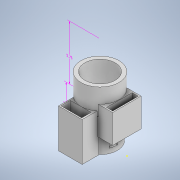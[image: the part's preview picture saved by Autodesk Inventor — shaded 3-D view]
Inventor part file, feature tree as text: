
AUTODESK INVENTOR PART (.ipt)
format: ipt  version: 2021 (Build 250183000, 183)  size: 472,064 bytes
history: native  units: in
note: dims shown in document units (in); Inventor stores cm internally (conversion verified against a paired STEP export)
features: sketch x24, extrude x14, other x3, plane x3, fillet x1
ambient origin geometry x8: Origin, YZ Plane, XZ Plane, XY Plane, X Axis, Y Axis, Z Axis, Center Point
bodies: Solid1 (feature_tree)
feature tree (45):
  other  "Annotations"
  extrude  "Extrusion1"  Depth=3.5433in TaperAngle=0.0deg
  extrude  "Extrusion2"  Depth=5.75in TaperAngle=0.0deg
  sketch  "Sketch4"  dims[d34=5.575in d35=0.0in d58=0.0787in]
  sketch  "Sketch5"  dims[d59=1.25in d60=4.1in]
  sketch  "Sketch6"  dims[d61=1.25in d62=4.1in]
  fillet  "Fillet1"  Radius=3.2in
  plane  "Work Plane2"
  extrude  "Extrusion4"  Depth=0.6875in TaperAngle=0.0deg
  sketch  "Sketch12"  dims[d67=2.2in d68=1.0in]
  sketch  "Sketch13"  dims[d69=3.8625in d70=0.0in d71=1.0in]
  extrude  "Extrusion8"  Depth=0.0787in
  plane  "Work Plane4"
  sketch  "Sketch24"  dims[d74=1.825in d75=0.0in d76=1.25in]
  extrude  "Extrusion13"  Depth=4.1in
  extrude  "Extrusion14"  Depth=4.1in
  sketch  "Sketch27"  dims[d81=1.0in d82=0.0in d83=1.875in d84=0.0in]
  sketch  "Sketch28"  dims[d85=0.65in]
  extrude  "Extrusion15"  Depth=1.7625in TaperAngle=0.0deg
  extrude  "Extrusion16"  Depth=1.0in
  plane  "Work Plane5"
  extrude  "Extrusion17"  Depth=1.0in
  sketch  "Sketch32"  dims[d91=3.0in d92=0.0in]
  extrude  "Extrusion18"  Depth=1.5in
  extrude  "Extrusion3"  Depth=1.25in
  extrude  "Extrusion19"  Depth=1.5in
  sketch  "Sketch35"  dims[d18=0.0344in]
  extrude  "Extrusion20"  Depth=1.5in
  extrude  "Extrusion21"  Depth=1.875in TaperAngle=0.0deg
  sketch  "Sketch1"  dims[d0=3.6614in d1=3.5433in d2=0.0in]
  sketch  "Sketch2"  dims[d3=4.0in d4=5.75in d5=0.0in d6=3.2in]
  sketch  "Sketch3"  dims[d7=9.0in d8=0.0in d11=0.6875in d12=0.0in]
  sketch  "Sketch7"  dims[d63=1.3in d64=0.0in d65=1.7625in d66=0.0in]
  sketch  "Sketch14"  dims[d72=0.6in d73=1.5in]
  sketch  "Sketch25"  dims[d77=3.0in d78=1.5in]
  sketch  "Sketch26"  dims[d79=3.0in d80=1.5in]
  sketch  "Sketch29"  dims[d86=2.7in]
  sketch  "Sketch30"  dims[d87=2.8125in d88=0.0in]
  sketch  "Sketch31"  dims[d89=2.8125in d90=0.0in]
  sketch  "Sketch33"  dims[d10=5.75in d9=3.5433in]
  sketch  "Sketch34"  dims[d17=0.5in]
  sketch  "Sketch36"  dims[d19=0.5in]
  sketch  "Sketch37"  dims[d20=0.0344in]
  other  "Linear Dimension 1"
  other  "Linear Dimension 2"
